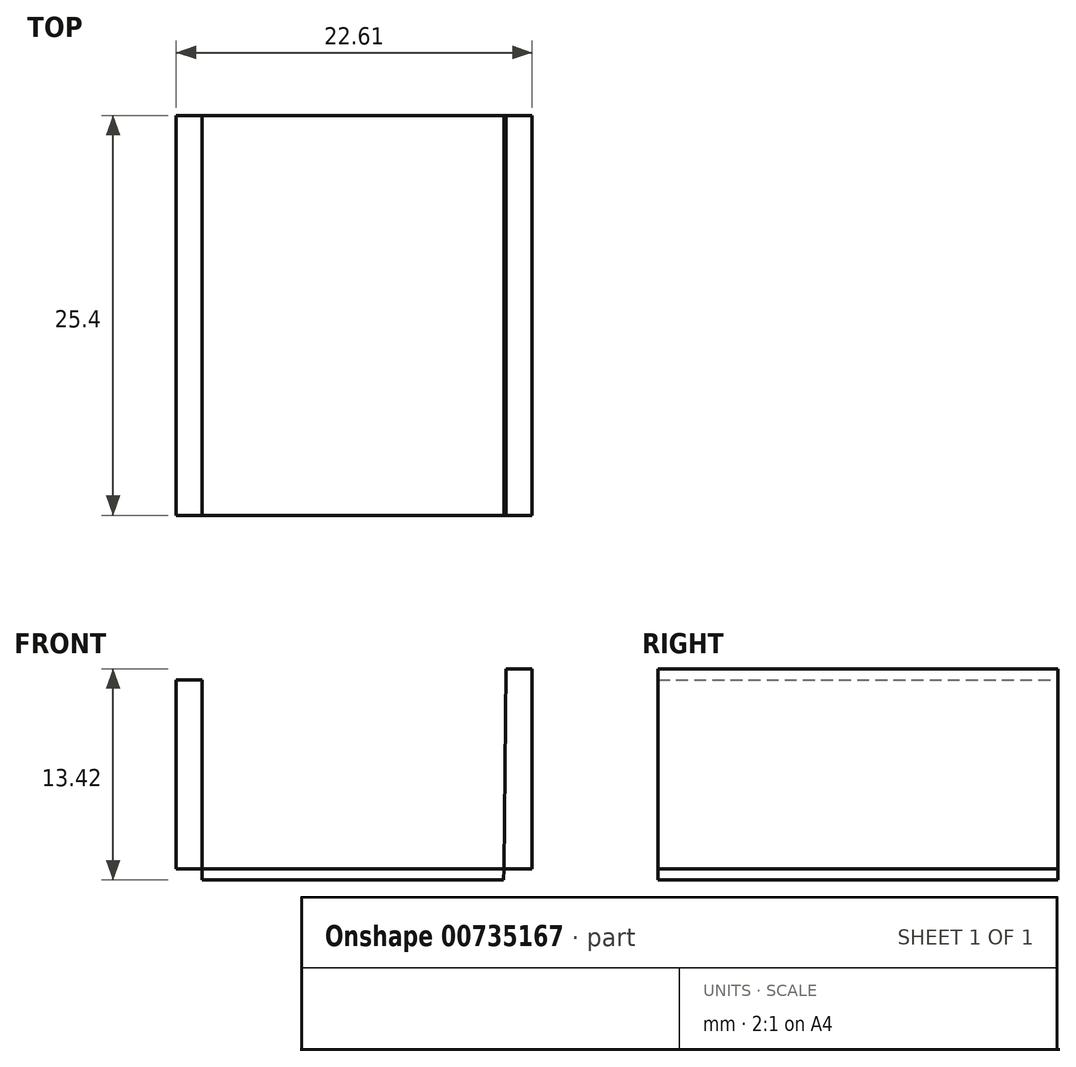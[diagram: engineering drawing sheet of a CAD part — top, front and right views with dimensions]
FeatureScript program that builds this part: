
annotation { "Feature Type Name" : "Feature", "Feature Type Description" : "" }
export const myFeature = defineFeature(function(context is Context, id is Id, definition is map)
    precondition{}
    {
        {
            var Q0;
            Q0=qCreatedBy(makeId("Front.planeOp"),FACE);
            var sketch = newSketch(context, id + "F0", { "sketchPlane" : qUnion([Q0])});
            skLineSegment(sketch, "E0", {"start": v(-9.95, 15.05) * mm, "end": v(-9.95, 2.35) * mm});
            skLineSegment(sketch, "E1", {"start": v(-8.3, 15.05) * mm, "end": v(-8.3, 2.35) * mm});
            skLineSegment(sketch, "E2", {"start": v(-9.95, 15.05) * mm, "end": v(-8.3, 15.05) * mm});
            skLineSegment(sketch, "E3", {"start": v(-9.95, 2.35) * mm, "end": v(8.18, 2.35) * mm});
            skLineSegment(sketch, "E4", {"start": v(-9.95, 3.07) * mm, "end": v(12.66, 3.07) * mm});
            skLineSegment(sketch, "E5", {"start": v(8.18, 2.35) * mm, "end": v(10.85, 2.35) * mm});
            skLineSegment(sketch, "E6", {"start": v(12.66, 3.07) * mm, "end": v(12.66, 15.77) * mm});
            skLineSegment(sketch, "E7", {"start": v(12.66, 15.77) * mm, "end": v(11.01, 15.77) * mm});
            skLineSegment(sketch, "E8", {"start": v(11.01, 15.77) * mm, "end": v(10.85, 2.35) * mm});
            skLineSegment(sketch, "E9", {"start": v(-9.95, 3.07) * mm, "end": v(-9.95, 2.35) * mm});
            skSolve(sketch);
        }
        {
            var Q0;
            {var subQ5=sQuery(id+"F0.wireOp",EDGE,"E5");Q0=makeQuery(id+"F0.imprint","IMPRINT",FACE,{"disambiguationData":[TD([[makeQuery(id+"F0.imprint","IMPRINT",EDGE,{"derivedFrom":subQ5}),1.0]])]});}
            var Q1;
            {var subQ0=sQuery(id+"F0.wireOp",EDGE,"E2");Q1=makeQuery(id+"F0.imprint","IMPRINT",FACE,{"disambiguationData":[TD([[makeQuery(id+"F0.imprint","IMPRINT",EDGE,{"derivedFrom":subQ0}),-1.0]])]});}
            var Q2;
            {var subQ0=sQuery(id+"F0.wireOp",EDGE,"E6");Q2=makeQuery(id+"F0.imprint","IMPRINT",FACE,{"disambiguationData":[TD([[makeQuery(id+"F0.imprint","IMPRINT",EDGE,{"derivedFrom":subQ0}),1.0]])]});}
            extrude(context, id + "F1", {"entities" : qUnion([Q0, Q1, Q2]), "depth" : 25.4 * mm, "offsetDistance" : 25.4 * mm});
        }
    });
